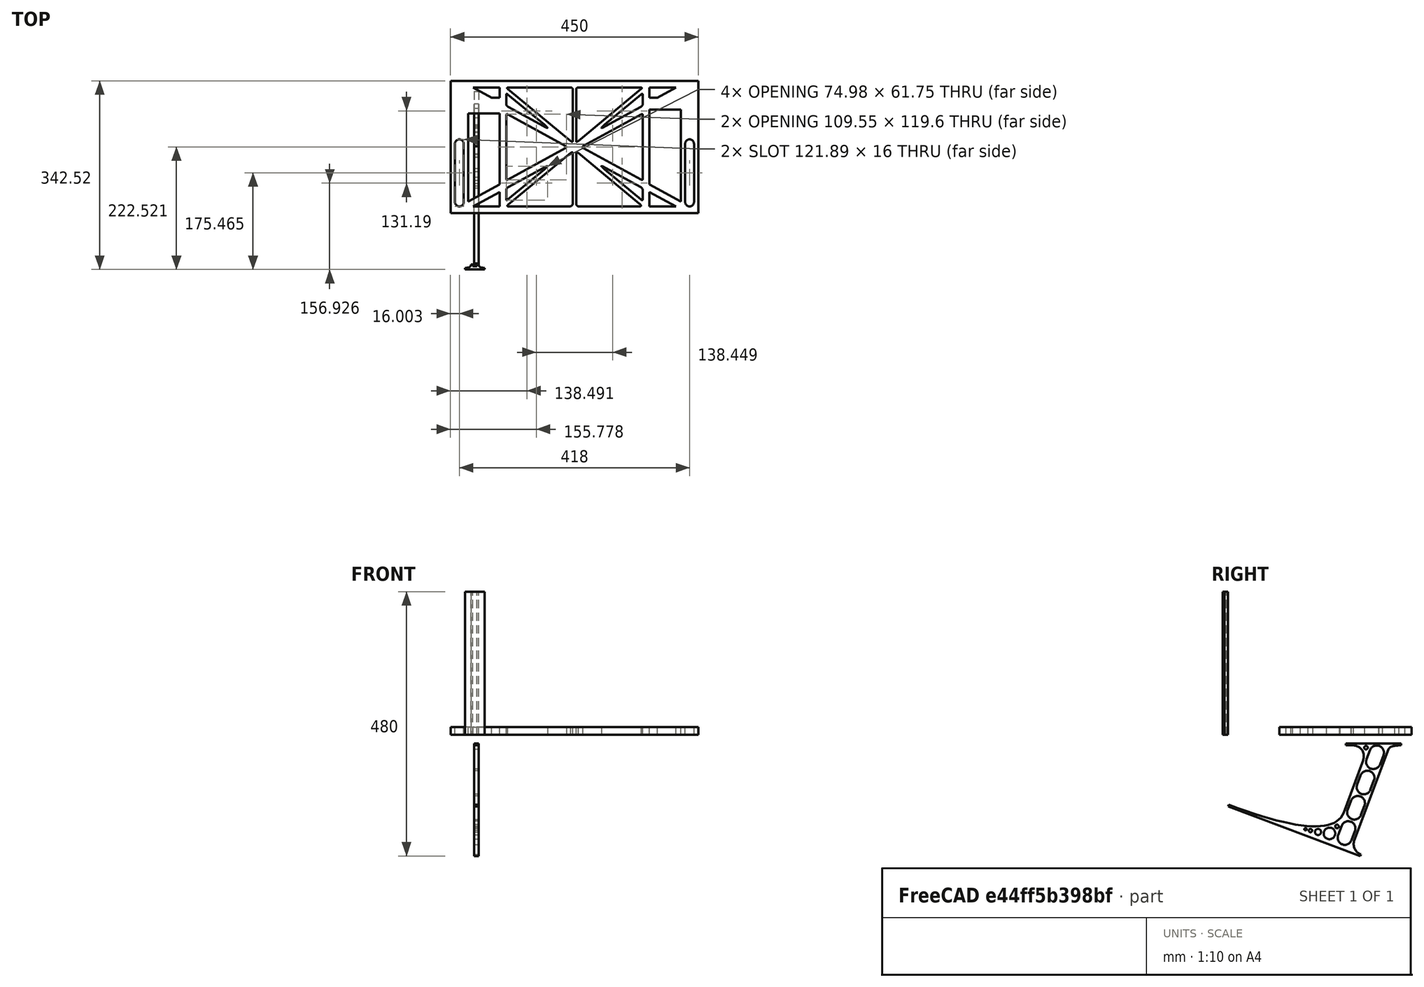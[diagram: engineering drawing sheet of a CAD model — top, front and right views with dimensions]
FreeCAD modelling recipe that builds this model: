
FCSTD DOCUMENT  (FreeCAD 0.19R0.19.2)
Label: laptopStand098
License: All rights reserved
LicenseURL: http://en.wikipedia.org/wiki/All_rights_reserved
objects: Sketcher::SketchObject×3, Part::Extrusion×3
note: 6 computed .brp shape members not serialized (recipe doc carries the construction recipe); baked Part::Feature solids carry a one-line shape summary decoded from their .brp

FEATURE [Sketcher::SketchObject] Sketch
  FullyConstrained = false
  sketch-geometry (276):
    g0: LineSegment StartX=-10.9272 StartY=-82.7794 StartZ=0 EndX=46.0728 EndY=-51.4823 EndZ=0
    g1: LineSegment StartX=366.073 StartY=-91.7794 StartZ=0 EndX=318.073 EndY=-65.424 EndZ=0
    g2: LineSegment StartX=-10.9272 StartY=77.3346 StartZ=0 EndX=-10.9272 EndY=-82.7794 EndZ=0
    g3: LineSegment StartX=375.073 StartY=-82.7794 StartZ=0 EndX=375.073 EndY=83.9235 EndZ=0
    g4: LineSegment StartX=-1.92719 StartY=-91.7794 StartZ=0 EndX=46.0728 EndY=-91.7794 EndZ=0
    g5: LineSegment StartX=318.073 StartY=124.221 StartZ=0 EndX=366.073 EndY=124.221 EndZ=0
    g6: LineSegment StartX=318.073 StartY=83.9235 StartZ=0 EndX=318.073 EndY=-51.4823 EndZ=0
    g7: LineSegment StartX=318.073 StartY=-51.4823 StartZ=0 EndX=375.073 EndY=-82.7794 EndZ=0
    g8: LineSegment StartX=318.073 StartY=-65.424 StartZ=0 EndX=318.073 EndY=-91.7794 EndZ=0
    g9: LineSegment StartX=318.073 StartY=-91.7794 StartZ=0 EndX=366.073 EndY=-91.7794 EndZ=0
    g10: LineSegment StartX=46.0728 StartY=-65.424 StartZ=0 EndX=-1.92719 EndY=-91.7794 EndZ=0
    g11: LineSegment StartX=46.0728 StartY=-65.424 StartZ=0 EndX=46.0728 EndY=-91.7794 EndZ=0
    g12: LineSegment StartX=46.0728 StartY=77.3346 StartZ=0 EndX=46.0728 EndY=-51.4823 EndZ=0
    g13: LineSegment StartX=-42.9272 StartY=136.221 StartZ=0 EndX=-42.9272 EndY=-103.779 EndZ=0
    g14: LineSegment StartX=407.073 StartY=136.221 StartZ=0 EndX=407.073 EndY=-103.779 EndZ=0
    g15: ArcOfCircle CenterX=-26.9272 CenterY=22.1087 CenterZ=0 NormalX=0 NormalY=0 NormalZ=1 AngleXU=0 Radius=8 StartAngle=1e-16 EndAngle=3.14159
    g16: ArcOfCircle CenterX=-26.9272 CenterY=-83.7794 CenterZ=0 NormalX=0 NormalY=0 NormalZ=1 AngleXU=0 Radius=8 StartAngle=3.14159 EndAngle=6.28319
    g17: LineSegment StartX=-34.9272 StartY=22.1087 StartZ=0 EndX=-34.9272 EndY=-83.7794 EndZ=0
    g18: LineSegment StartX=-18.9272 StartY=22.1087 StartZ=0 EndX=-18.9272 EndY=-83.7794 EndZ=0
    g19: ArcOfCircle CenterX=391.073 CenterY=22.1087 CenterZ=0 NormalX=0 NormalY=0 NormalZ=1 AngleXU=0 Radius=8 StartAngle=-4.4e-15 EndAngle=3.14159
    g20: LineSegment StartX=399.073 StartY=22.1087 StartZ=0 EndX=399.073 EndY=-83.7794 EndZ=0
    g21: LineSegment StartX=383.073 StartY=22.1087 StartZ=0 EndX=383.073 EndY=-83.7794 EndZ=0
    g22: ArcOfCircle CenterX=391.073 CenterY=-83.7794 CenterZ=0 NormalX=0 NormalY=0 NormalZ=1 AngleXU=0 Radius=8 StartAngle=3.14159 EndAngle=6.28319
    g23: Circle CenterX=175.022 CenterY=27.0628 CenterZ=0 NormalX=0 NormalY=0 NormalZ=1 AngleXU=0 Radius=1
    g24: Circle CenterX=179.022 CenterY=24.8665 CenterZ=0 NormalX=0 NormalY=0 NormalZ=1 AngleXU=0 Radius=1
    g25: Circle CenterX=179.022 CenterY=27.0628 CenterZ=0 NormalX=0 NormalY=0 NormalZ=1 AngleXU=0 Radius=1
    g26: BSplineCurve PolesCount=3 KnotsCount=2 Degree=2 IsPeriodic=0
    g27: GeomPoint X=175.022 Y=27.0628 Z=0
    g28: GeomPoint X=179.022 Y=27.0628 Z=0
    g29: Circle CenterX=189.124 CenterY=27.0628 CenterZ=0 NormalX=0 NormalY=0 NormalZ=1 AngleXU=0 Radius=1
    g30: Circle CenterX=185.124 CenterY=24.8665 CenterZ=0 NormalX=0 NormalY=0 NormalZ=1 AngleXU=0 Radius=1
    g31: Circle CenterX=185.124 CenterY=27.0628 CenterZ=0 NormalX=0 NormalY=0 NormalZ=1 AngleXU=0 Radius=1
    g32: BSplineCurve PolesCount=3 KnotsCount=2 Degree=2 IsPeriodic=0
    g33: GeomPoint X=189.124 Y=27.0628 Z=0
    g34: GeomPoint X=185.124 Y=27.0628 Z=0
    g35: Circle CenterX=175.022 CenterY=5.37834 CenterZ=0 NormalX=0 NormalY=0 NormalZ=1 AngleXU=0 Radius=1
    g36: Circle CenterX=179.022 CenterY=7.57463 CenterZ=0 NormalX=0 NormalY=0 NormalZ=1 AngleXU=0 Radius=1
    g37: Circle CenterX=179.022 CenterY=5.34704 CenterZ=0 NormalX=0 NormalY=0 NormalZ=1 AngleXU=0 Radius=1
    g38: BSplineCurve PolesCount=3 KnotsCount=2 Degree=2 IsPeriodic=0
    g39: GeomPoint X=175.022 Y=5.37834 Z=0
    g40: GeomPoint X=179.022 Y=5.34704 Z=0
    g41: Circle CenterX=189.124 CenterY=5.37834 CenterZ=0 NormalX=0 NormalY=0 NormalZ=1 AngleXU=0 Radius=1
    g42: Circle CenterX=185.124 CenterY=7.57463 CenterZ=0 NormalX=0 NormalY=0 NormalZ=1 AngleXU=0 Radius=1
    g43: Circle CenterX=185.124 CenterY=5.34704 CenterZ=0 NormalX=0 NormalY=0 NormalZ=1 AngleXU=0 Radius=1
    g44: BSplineCurve PolesCount=3 KnotsCount=2 Degree=2 IsPeriodic=0
    g45: GeomPoint X=189.124 Y=5.37834 Z=0
    g46: GeomPoint X=185.124 Y=5.34704 Z=0
    g47: Circle CenterX=165.871 CenterY=18.1458 CenterZ=0 NormalX=0 NormalY=0 NormalZ=1 AngleXU=0 Radius=1
    g48: Circle CenterX=169.377 CenterY=16.2206 CenterZ=0 NormalX=0 NormalY=0 NormalZ=1 AngleXU=0 Radius=1
    g49: Circle CenterX=165.871 CenterY=14.2954 CenterZ=0 NormalX=0 NormalY=0 NormalZ=1 AngleXU=0 Radius=1
    g50: BSplineCurve PolesCount=3 KnotsCount=2 Degree=2 IsPeriodic=0
    g51: GeomPoint X=165.871 Y=18.1458 Z=0
    g52: GeomPoint X=165.871 Y=14.2954 Z=0
    g53: Circle CenterX=198.275 CenterY=18.1458 CenterZ=0 NormalX=0 NormalY=0 NormalZ=1 AngleXU=0 Radius=1
    g54: Circle CenterX=194.768 CenterY=16.2206 CenterZ=0 NormalX=0 NormalY=0 NormalZ=1 AngleXU=0 Radius=1
    g55: Circle CenterX=198.275 CenterY=14.2954 CenterZ=0 NormalX=0 NormalY=0 NormalZ=1 AngleXU=0 Radius=1
    g56: BSplineCurve PolesCount=3 KnotsCount=2 Degree=2 IsPeriodic=0
    g57: GeomPoint X=198.275 Y=18.1458 Z=0
    g58: GeomPoint X=198.275 Y=14.2954 Z=0
    g59: LineSegment StartX=407.073 StartY=-103.779 StartZ=0 EndX=-42.9272 EndY=-103.779 EndZ=0
    g60: LineSegment StartX=407.073 StartY=136.221 StartZ=0 EndX=-42.9272 EndY=136.221 EndZ=0
    g61: LineSegment StartX=46.0728 StartY=77.3346 StartZ=0 EndX=-10.9272 EndY=77.3346 EndZ=0
    g62: LineSegment StartX=46.0728 StartY=105.865 StartZ=0 EndX=31.5028 EndY=105.865 EndZ=0
    g63: LineSegment StartX=46.0728 StartY=124.221 StartZ=0 EndX=46.0728 EndY=105.865 EndZ=0
    g64: LineSegment StartX=-1.92719 StartY=124.221 StartZ=0 EndX=31.5028 EndY=105.865 EndZ=0
    g65: LineSegment StartX=46.0728 StartY=124.221 StartZ=0 EndX=-1.92719 EndY=124.221 EndZ=0
    g66: LineSegment StartX=318.073 StartY=83.9235 StartZ=0 EndX=375.073 EndY=83.9235 EndZ=0
    g67: Circle CenterX=125.607 CenterY=54.1951 CenterZ=0 NormalX=0 NormalY=0 NormalZ=1 AngleXU=0 Radius=1
    g68: Circle CenterX=139.632 CenterY=46.4944 CenterZ=0 NormalX=0 NormalY=0 NormalZ=1 AngleXU=0 Radius=1
    g69: Circle CenterX=127.326 CenterY=56.7187 CenterZ=0 NormalX=0 NormalY=0 NormalZ=1 AngleXU=0 Radius=1
    g70: BSplineCurve PolesCount=3 KnotsCount=2 Degree=2 IsPeriodic=0
    g71: GeomPoint X=125.607 Y=54.1951 Z=0
    g72: GeomPoint X=127.326 Y=56.7187 Z=0
    g73: Circle CenterX=236.821 CenterY=56.7187 CenterZ=0 NormalX=0 NormalY=0 NormalZ=1 AngleXU=0 Radius=1
    g74: Circle CenterX=224.513 CenterY=46.4944 CenterZ=0 NormalX=0 NormalY=0 NormalZ=1 AngleXU=0 Radius=1
    g75: Circle CenterX=238.538 CenterY=54.1951 CenterZ=0 NormalX=0 NormalY=0 NormalZ=1 AngleXU=0 Radius=1
    g76: BSplineCurve PolesCount=3 KnotsCount=2 Degree=2 IsPeriodic=0
    g77: GeomPoint X=236.821 Y=56.7187 Z=0
    g78: GeomPoint X=238.538 Y=54.1951 Z=0
    g79: Circle CenterX=238.538 CenterY=-21.7539 CenterZ=0 NormalX=0 NormalY=0 NormalZ=1 AngleXU=0 Radius=1
    g80: Circle CenterX=224.513 CenterY=-14.0532 CenterZ=0 NormalX=0 NormalY=0 NormalZ=1 AngleXU=0 Radius=1
    g81: Circle CenterX=236.821 CenterY=-24.2775 CenterZ=0 NormalX=0 NormalY=0 NormalZ=1 AngleXU=0 Radius=1
    g82: BSplineCurve PolesCount=3 KnotsCount=2 Degree=2 IsPeriodic=0
    g83: GeomPoint X=238.538 Y=-21.7539 Z=0
    g84: GeomPoint X=236.821 Y=-24.2775 Z=0
    g85: Circle CenterX=125.607 CenterY=-21.7539 CenterZ=0 NormalX=0 NormalY=0 NormalZ=1 AngleXU=0 Radius=1
    g86: Circle CenterX=139.632 CenterY=-14.0532 CenterZ=0 NormalX=0 NormalY=0 NormalZ=1 AngleXU=0 Radius=1
    g87: Circle CenterX=127.325 CenterY=-24.2775 CenterZ=0 NormalX=0 NormalY=0 NormalZ=1 AngleXU=0 Radius=1
    g88: BSplineCurve PolesCount=3 KnotsCount=2 Degree=2 IsPeriodic=0
    g89: GeomPoint X=125.607 Y=-21.7539 Z=0
    g90: GeomPoint X=127.325 Y=-24.2775 Z=0
    g91: Circle CenterX=302.996 CenterY=111.695 CenterZ=0 NormalX=0 NormalY=0 NormalZ=1 AngleXU=0 Radius=1
    g92: Circle CenterX=306.073 CenterY=114.251 CenterZ=0 NormalX=0 NormalY=0 NormalZ=1 AngleXU=0 Radius=1
    g93: Circle CenterX=306.073 CenterY=110.251 CenterZ=0 NormalX=0 NormalY=0 NormalZ=1 AngleXU=0 Radius=1
    g94: BSplineCurve PolesCount=3 KnotsCount=2 Degree=2 IsPeriodic=0
    g95: GeomPoint X=302.996 Y=111.695 Z=0
    g96: GeomPoint X=306.073 Y=110.251 Z=0
    g97: Circle CenterX=306.073 CenterY=95.2763 CenterZ=0 NormalX=0 NormalY=0 NormalZ=1 AngleXU=0 Radius=1
    g98: Circle CenterX=306.073 CenterY=91.2763 CenterZ=0 NormalX=0 NormalY=0 NormalZ=1 AngleXU=0 Radius=1
    g99: Circle CenterX=302.567 CenterY=89.3511 CenterZ=0 NormalX=0 NormalY=0 NormalZ=1 AngleXU=0 Radius=1
    g100: BSplineCurve PolesCount=3 KnotsCount=2 Degree=2 IsPeriodic=0
    g101: GeomPoint X=306.073 Y=95.2763 Z=0
    g102: GeomPoint X=302.567 Y=89.3511 Z=0
    g103: LineSegment StartX=306.073 StartY=110.251 StartZ=0 EndX=306.073 EndY=95.2763 EndZ=0
    g104: LineSegment StartX=302.996 StartY=111.695 StartZ=0 EndX=236.821 EndY=56.7187 EndZ=0
    g105: LineSegment StartX=238.538 StartY=54.1951 StartZ=0 EndX=302.567 EndY=89.3511 EndZ=0
    g106: Circle CenterX=61.1496 CenterY=111.695 CenterZ=0 NormalX=0 NormalY=0 NormalZ=1 AngleXU=0 Radius=1
    g107: Circle CenterX=58.0728 CenterY=114.251 CenterZ=0 NormalX=0 NormalY=0 NormalZ=1 AngleXU=0 Radius=1
    g108: Circle CenterX=58.0728 CenterY=110.251 CenterZ=0 NormalX=0 NormalY=0 NormalZ=1 AngleXU=0 Radius=1
    g109: BSplineCurve PolesCount=3 KnotsCount=2 Degree=2 IsPeriodic=0
    g110: GeomPoint X=61.1496 Y=111.695 Z=0
    g111: GeomPoint X=58.0728 Y=110.251 Z=0
    g112: Circle CenterX=61.5791 CenterY=89.3511 CenterZ=0 NormalX=0 NormalY=0 NormalZ=1 AngleXU=0 Radius=1
    g113: Circle CenterX=58.0728 CenterY=91.2763 CenterZ=0 NormalX=0 NormalY=0 NormalZ=1 AngleXU=0 Radius=1
    g114: Circle CenterX=58.0728 CenterY=95.2763 CenterZ=0 NormalX=0 NormalY=0 NormalZ=1 AngleXU=0 Radius=1
    g115: BSplineCurve PolesCount=3 KnotsCount=2 Degree=2 IsPeriodic=0
    g116: GeomPoint X=61.5791 Y=89.3511 Z=0
    g117: GeomPoint X=58.0728 Y=95.2763 Z=0
    g118: LineSegment StartX=58.0728 StartY=110.251 StartZ=0 EndX=58.0728 EndY=95.2763 EndZ=0
    g119: LineSegment StartX=61.1496 StartY=111.695 StartZ=0 EndX=127.326 EndY=56.7187 EndZ=0
    g120: LineSegment StartX=125.607 StartY=54.1951 StartZ=0 EndX=61.5791 EndY=89.3511 EndZ=0
    g121: Circle CenterX=61.5791 CenterY=-56.9099 CenterZ=0 NormalX=0 NormalY=0 NormalZ=1 AngleXU=0 Radius=1
    g122: Circle CenterX=58.0728 CenterY=-58.8351 CenterZ=0 NormalX=0 NormalY=0 NormalZ=1 AngleXU=0 Radius=1
    g123: Circle CenterX=58.0728 CenterY=-62.8351 CenterZ=0 NormalX=0 NormalY=0 NormalZ=1 AngleXU=0 Radius=1
    g124: BSplineCurve PolesCount=3 KnotsCount=2 Degree=2 IsPeriodic=0
    g125: GeomPoint X=61.5791 Y=-56.9099 Z=0
    g126: GeomPoint X=58.0728 Y=-62.8351 Z=0
    g127: Circle CenterX=58.0728 CenterY=-77.8102 CenterZ=0 NormalX=0 NormalY=0 NormalZ=1 AngleXU=0 Radius=1
    g128: Circle CenterX=58.0728 CenterY=-81.8102 CenterZ=0 NormalX=0 NormalY=0 NormalZ=1 AngleXU=0 Radius=1
    g129: Circle CenterX=61.1496 CenterY=-79.2541 CenterZ=0 NormalX=0 NormalY=0 NormalZ=1 AngleXU=0 Radius=1
    g130: BSplineCurve PolesCount=3 KnotsCount=2 Degree=2 IsPeriodic=0
    g131: GeomPoint X=58.0728 Y=-77.8102 Z=0
    g132: GeomPoint X=61.1496 Y=-79.2541 Z=0
    g133: LineSegment StartX=58.0728 StartY=-62.8351 StartZ=0 EndX=58.0728 EndY=-77.8102 EndZ=0
    g134: LineSegment StartX=61.1496 StartY=-79.2541 StartZ=0 EndX=127.325 EndY=-24.2775 EndZ=0
    g135: LineSegment StartX=125.607 StartY=-21.7539 StartZ=0 EndX=61.5791 EndY=-56.9099 EndZ=0
    g136: Circle CenterX=302.567 CenterY=-56.9099 CenterZ=0 NormalX=0 NormalY=0 NormalZ=1 AngleXU=0 Radius=1
    g137: Circle CenterX=306.073 CenterY=-58.8351 CenterZ=0 NormalX=0 NormalY=0 NormalZ=1 AngleXU=0 Radius=1
    g138: Circle CenterX=306.073 CenterY=-62.8351 CenterZ=0 NormalX=0 NormalY=0 NormalZ=1 AngleXU=0 Radius=1
    g139: BSplineCurve PolesCount=3 KnotsCount=2 Degree=2 IsPeriodic=0
    g140: GeomPoint X=302.567 Y=-56.9099 Z=0
    g141: GeomPoint X=306.073 Y=-62.8351 Z=0
    g142: Circle CenterX=302.996 CenterY=-79.2541 CenterZ=0 NormalX=0 NormalY=0 NormalZ=1 AngleXU=0 Radius=1
    g143: Circle CenterX=306.073 CenterY=-81.8102 CenterZ=0 NormalX=0 NormalY=0 NormalZ=1 AngleXU=0 Radius=1
    g144: Circle CenterX=306.073 CenterY=-77.8102 CenterZ=0 NormalX=0 NormalY=0 NormalZ=1 AngleXU=0 Radius=1
    g145: BSplineCurve PolesCount=3 KnotsCount=2 Degree=2 IsPeriodic=0
    g146: GeomPoint X=302.996 Y=-79.2541 Z=0
    g147: GeomPoint X=306.073 Y=-77.8102 Z=0
    g148: LineSegment StartX=306.073 StartY=-62.8351 StartZ=0 EndX=306.073 EndY=-77.8102 EndZ=0
    g149: LineSegment StartX=302.996 StartY=-79.2541 StartZ=0 EndX=236.821 EndY=-24.2775 EndZ=0
    g150: LineSegment StartX=238.538 StartY=-21.7539 StartZ=0 EndX=302.567 EndY=-56.9099 EndZ=0
    g151: Circle CenterX=61.6457 CenterY=-88.8112 CenterZ=0 NormalX=0 NormalY=0 NormalZ=1 AngleXU=0 Radius=1
    g152: Circle CenterX=58.0728 CenterY=-91.7794 CenterZ=0 NormalX=0 NormalY=0 NormalZ=1 AngleXU=0 Radius=1
    g153: Circle CenterX=63.9135 CenterY=-91.7794 CenterZ=0 NormalX=0 NormalY=0 NormalZ=1 AngleXU=0 Radius=1
    g154: BSplineCurve PolesCount=3 KnotsCount=2 Degree=2 IsPeriodic=0
    g155: GeomPoint X=61.6457 Y=-88.8112 Z=0
    g156: GeomPoint X=63.9135 Y=-91.7794 Z=0
    g157: Circle CenterX=179.022 CenterY=-85.8163 CenterZ=0 NormalX=0 NormalY=0 NormalZ=1 AngleXU=0 Radius=1
    g158: Circle CenterX=179.022 CenterY=-91.7794 CenterZ=0 NormalX=0 NormalY=0 NormalZ=1 AngleXU=0 Radius=1
    g159: Circle CenterX=171.895 CenterY=-91.7794 CenterZ=0 NormalX=0 NormalY=0 NormalZ=1 AngleXU=0 Radius=1
    g160: BSplineCurve PolesCount=3 KnotsCount=2 Degree=2 IsPeriodic=0
    g161: GeomPoint X=179.022 Y=-85.8163 Z=0
    g162: GeomPoint X=171.895 Y=-91.7794 Z=0
    g163: Circle CenterX=185.124 CenterY=-86.2028 CenterZ=0 NormalX=0 NormalY=0 NormalZ=1 AngleXU=0 Radius=1
    g164: Circle CenterX=185.124 CenterY=-91.7794 CenterZ=0 NormalX=0 NormalY=0 NormalZ=1 AngleXU=0 Radius=1
    g165: Circle CenterX=191.747 CenterY=-91.7794 CenterZ=0 NormalX=0 NormalY=0 NormalZ=1 AngleXU=0 Radius=1
    g166: BSplineCurve PolesCount=3 KnotsCount=2 Degree=2 IsPeriodic=0
    g167: GeomPoint X=185.124 Y=-86.2028 Z=0
    g168: GeomPoint X=191.747 Y=-91.7794 Z=0
    g169: Circle CenterX=299.888 CenterY=-86.6413 CenterZ=0 NormalX=0 NormalY=0 NormalZ=1 AngleXU=0 Radius=1
    g170: Circle CenterX=306.073 CenterY=-91.7794 CenterZ=0 NormalX=0 NormalY=0 NormalZ=1 AngleXU=0 Radius=1
    g171: Circle CenterX=298.776 CenterY=-91.7794 CenterZ=0 NormalX=0 NormalY=0 NormalZ=1 AngleXU=0 Radius=1
    g172: BSplineCurve PolesCount=3 KnotsCount=2 Degree=2 IsPeriodic=0
    g173: GeomPoint X=299.888 Y=-86.6413 Z=0
    g174: GeomPoint X=298.776 Y=-91.7794 Z=0
    g175: LineSegment StartX=189.124 StartY=5.37834 StartZ=0 EndX=299.888 EndY=-86.6413 EndZ=0
    g176: LineSegment StartX=298.776 StartY=-91.7794 StartZ=0 EndX=191.747 EndY=-91.7794 EndZ=0
    g177: LineSegment StartX=185.124 StartY=-86.2028 StartZ=0 EndX=185.124 EndY=5.34704 EndZ=0
    g178: LineSegment StartX=179.022 StartY=5.34704 StartZ=0 EndX=179.022 EndY=-85.8163 EndZ=0
    g179: LineSegment StartX=171.895 StartY=-91.7794 StartZ=0 EndX=63.9135 EndY=-91.7794 EndZ=0
    g180: LineSegment StartX=61.6457 StartY=-88.8112 StartZ=0 EndX=175.022 EndY=5.37834 EndZ=0
    g181: Circle CenterX=302.073 CenterY=124.221 CenterZ=0 NormalX=0 NormalY=0 NormalZ=1 AngleXU=0 Radius=1
    g182: Circle CenterX=306.073 CenterY=124.221 CenterZ=0 NormalX=0 NormalY=0 NormalZ=1 AngleXU=0 Radius=1
    g183: Circle CenterX=302.996 CenterY=121.665 CenterZ=0 NormalX=0 NormalY=0 NormalZ=1 AngleXU=0 Radius=1
    g184: BSplineCurve PolesCount=3 KnotsCount=2 Degree=2 IsPeriodic=0
    g185: GeomPoint X=302.073 Y=124.221 Z=0
    g186: GeomPoint X=302.996 Y=121.665 Z=0
    g187: Circle CenterX=189.124 CenterY=124.221 CenterZ=0 NormalX=0 NormalY=0 NormalZ=1 AngleXU=0 Radius=1
    g188: Circle CenterX=185.124 CenterY=124.221 CenterZ=0 NormalX=0 NormalY=0 NormalZ=1 AngleXU=0 Radius=1
    g189: Circle CenterX=185.124 CenterY=120.221 CenterZ=0 NormalX=0 NormalY=0 NormalZ=1 AngleXU=0 Radius=1
    g190: BSplineCurve PolesCount=3 KnotsCount=2 Degree=2 IsPeriodic=0
    g191: GeomPoint X=189.124 Y=124.221 Z=0
    g192: GeomPoint X=185.124 Y=120.221 Z=0
    g193: Circle CenterX=175.022 CenterY=124.221 CenterZ=0 NormalX=0 NormalY=0 NormalZ=1 AngleXU=0 Radius=1
    g194: Circle CenterX=179.022 CenterY=124.221 CenterZ=0 NormalX=0 NormalY=0 NormalZ=1 AngleXU=0 Radius=1
    g195: Circle CenterX=179.022 CenterY=120.221 CenterZ=0 NormalX=0 NormalY=0 NormalZ=1 AngleXU=0 Radius=1
    g196: BSplineCurve PolesCount=3 KnotsCount=2 Degree=2 IsPeriodic=0
    g197: GeomPoint X=175.022 Y=124.221 Z=0
    g198: GeomPoint X=179.022 Y=120.221 Z=0
    g199: Circle CenterX=62.0728 CenterY=124.221 CenterZ=0 NormalX=0 NormalY=0 NormalZ=1 AngleXU=0 Radius=1
    g200: Circle CenterX=58.0728 CenterY=124.221 CenterZ=0 NormalX=0 NormalY=0 NormalZ=1 AngleXU=0 Radius=1
    g201: Circle CenterX=61.1496 CenterY=121.665 CenterZ=0 NormalX=0 NormalY=0 NormalZ=1 AngleXU=0 Radius=1
    g202: BSplineCurve PolesCount=3 KnotsCount=2 Degree=2 IsPeriodic=0
    g203: GeomPoint X=62.0728 Y=124.221 Z=0
    g204: GeomPoint X=61.1496 Y=121.665 Z=0
    g205: LineSegment StartX=62.0728 StartY=124.221 StartZ=0 EndX=175.022 EndY=124.221 EndZ=0
    g206: LineSegment StartX=179.022 StartY=120.221 StartZ=0 EndX=179.022 EndY=27.0628 EndZ=0
    g207: LineSegment StartX=185.124 StartY=27.0628 StartZ=0 EndX=185.124 EndY=120.221 EndZ=0
    g208: LineSegment StartX=189.124 StartY=124.221 StartZ=0 EndX=302.073 EndY=124.221 EndZ=0
    g209: LineSegment StartX=302.996 StartY=121.665 StartZ=0 EndX=189.124 EndY=27.0628 EndZ=0
    g210: LineSegment StartX=175.022 StartY=27.0628 StartZ=0 EndX=61.1496 EndY=121.665 EndZ=0
    g211: Circle CenterX=61.5791 CenterY=75.4095 CenterZ=0 NormalX=0 NormalY=0 NormalZ=1 AngleXU=0 Radius=1
    g212: Circle CenterX=58.0728 CenterY=77.3346 CenterZ=0 NormalX=0 NormalY=0 NormalZ=1 AngleXU=0 Radius=1
    g213: Circle CenterX=58.0728 CenterY=73.3346 CenterZ=0 NormalX=0 NormalY=0 NormalZ=1 AngleXU=0 Radius=1
    g214: BSplineCurve PolesCount=3 KnotsCount=2 Degree=2 IsPeriodic=0
    g215: GeomPoint X=61.5791 Y=75.4095 Z=0
    g216: GeomPoint X=58.0728 Y=73.3346 Z=0
    g217: Circle CenterX=58.0728 CenterY=-40.8935 CenterZ=0 NormalX=0 NormalY=0 NormalZ=1 AngleXU=0 Radius=1
    g218: Circle CenterX=58.0728 CenterY=-44.8935 CenterZ=0 NormalX=0 NormalY=0 NormalZ=1 AngleXU=0 Radius=1
    g219: Circle CenterX=61.5791 CenterY=-42.9683 CenterZ=0 NormalX=0 NormalY=0 NormalZ=1 AngleXU=0 Radius=1
    g220: BSplineCurve PolesCount=3 KnotsCount=2 Degree=2 IsPeriodic=0
    g221: GeomPoint X=58.0728 Y=-40.8935 Z=0
    g222: GeomPoint X=61.5791 Y=-42.9683 Z=0
    g223: LineSegment StartX=61.5791 StartY=-42.9683 StartZ=0 EndX=165.871 EndY=14.2954 EndZ=0
    g224: LineSegment StartX=165.871 StartY=18.1458 StartZ=0 EndX=61.5791 EndY=75.4095 EndZ=0
    g225: LineSegment StartX=58.0728 StartY=73.3346 StartZ=0 EndX=58.0728 EndY=-40.8935 EndZ=0
    g226: Circle CenterX=302.567 CenterY=-42.9683 CenterZ=0 NormalX=0 NormalY=0 NormalZ=1 AngleXU=0 Radius=1
    g227: Circle CenterX=306.073 CenterY=-44.8935 CenterZ=0 NormalX=0 NormalY=0 NormalZ=1 AngleXU=0 Radius=1
    g228: Circle CenterX=306.073 CenterY=-40.8935 CenterZ=0 NormalX=0 NormalY=0 NormalZ=1 AngleXU=0 Radius=1
    g229: BSplineCurve PolesCount=3 KnotsCount=2 Degree=2 IsPeriodic=0
    g230: GeomPoint X=302.567 Y=-42.9683 Z=0
    g231: GeomPoint X=306.073 Y=-40.8935 Z=0
    g232: Circle CenterX=306.073 CenterY=73.3346 CenterZ=0 NormalX=0 NormalY=0 NormalZ=1 AngleXU=0 Radius=1
    g233: Circle CenterX=306.073 CenterY=77.3346 CenterZ=0 NormalX=0 NormalY=0 NormalZ=1 AngleXU=0 Radius=1
    g234: Circle CenterX=302.567 CenterY=75.4095 CenterZ=0 NormalX=0 NormalY=0 NormalZ=1 AngleXU=0 Radius=1
    g235: BSplineCurve PolesCount=3 KnotsCount=2 Degree=2 IsPeriodic=0
    g236: GeomPoint X=306.073 Y=73.3346 Z=0
    g237: GeomPoint X=302.567 Y=75.4095 Z=0
    g238: LineSegment StartX=302.567 StartY=-42.9683 StartZ=0 EndX=198.275 EndY=14.2954 EndZ=0
    g239: LineSegment StartX=198.275 StartY=18.1458 StartZ=0 EndX=302.567 EndY=75.4095 EndZ=0
    g240: LineSegment StartX=306.073 StartY=73.3346 StartZ=0 EndX=306.073 EndY=-40.8935 EndZ=0
    g241: LineSegment StartX=318.073 StartY=124.221 StartZ=0 EndX=322.073 EndY=124.221 EndZ=0
    g242: LineSegment StartX=366.073 StartY=124.221 StartZ=0 EndX=362.073 EndY=124.221 EndZ=0
    g243: LineSegment StartX=328.643 StartY=105.865 StartZ=0 EndX=332.643 EndY=105.865 EndZ=0
    g244: LineSegment StartX=332.651 StartY=105.853 StartZ=0 EndX=336.157 EndY=107.779 EndZ=0
    g245: LineSegment StartX=366.073 StartY=124.221 StartZ=0 EndX=362.567 EndY=122.294 EndZ=0
    g246: LineSegment StartX=318.073 StartY=105.865 StartZ=0 EndX=318.073 EndY=109.865 EndZ=0
    g247: LineSegment StartX=318.073 StartY=105.865 StartZ=0 EndX=322.073 EndY=105.865 EndZ=0
    g248: LineSegment StartX=318.073 StartY=124.221 StartZ=0 EndX=318.073 EndY=120.221 EndZ=0
    g249: LineSegment StartX=322.073 StartY=105.865 StartZ=0 EndX=328.643 EndY=105.865 EndZ=0
    g250: LineSegment StartX=318.073 StartY=120.221 StartZ=0 EndX=318.073 EndY=109.865 EndZ=0
    g251: LineSegment StartX=336.157 StartY=107.779 StartZ=0 EndX=362.567 EndY=122.294 EndZ=0
    g252: Circle CenterX=362.073 CenterY=124.221 CenterZ=0 NormalX=0 NormalY=0 NormalZ=1 AngleXU=0 Radius=1
    g253: Circle CenterX=366.073 CenterY=124.221 CenterZ=0 NormalX=0 NormalY=0 NormalZ=1 AngleXU=0 Radius=1
    g254: Circle CenterX=362.567 CenterY=122.294 CenterZ=0 NormalX=0 NormalY=0 NormalZ=1 AngleXU=0 Radius=1
    g255: BSplineCurve PolesCount=3 KnotsCount=2 Degree=2 IsPeriodic=0
    g256: GeomPoint X=362.073 Y=124.221 Z=0
    g257: GeomPoint X=362.567 Y=122.294 Z=0
    g258: Circle CenterX=322.073 CenterY=124.221 CenterZ=0 NormalX=0 NormalY=0 NormalZ=1 AngleXU=0 Radius=1
    g259: Circle CenterX=318.073 CenterY=124.221 CenterZ=0 NormalX=0 NormalY=0 NormalZ=1 AngleXU=0 Radius=1
    g260: Circle CenterX=318.073 CenterY=120.221 CenterZ=0 NormalX=0 NormalY=0 NormalZ=1 AngleXU=0 Radius=1
    g261: BSplineCurve PolesCount=3 KnotsCount=2 Degree=2 IsPeriodic=0
    g262: GeomPoint X=322.073 Y=124.221 Z=0
    g263: GeomPoint X=318.073 Y=120.221 Z=0
    g264: Circle CenterX=322.073 CenterY=105.865 CenterZ=0 NormalX=0 NormalY=0 NormalZ=1 AngleXU=0 Radius=1
    g265: Circle CenterX=318.073 CenterY=105.865 CenterZ=0 NormalX=0 NormalY=0 NormalZ=1 AngleXU=0 Radius=1
    g266: Circle CenterX=318.073 CenterY=109.865 CenterZ=0 NormalX=0 NormalY=0 NormalZ=1 AngleXU=0 Radius=1
    g267: BSplineCurve PolesCount=3 KnotsCount=2 Degree=2 IsPeriodic=0
    g268: GeomPoint X=322.073 Y=105.865 Z=0
    g269: GeomPoint X=318.073 Y=109.865 Z=0
    g270: Circle CenterX=336.157 CenterY=107.779 CenterZ=0 NormalX=0 NormalY=0 NormalZ=1 AngleXU=0 Radius=1
    g271: Circle CenterX=332.651 CenterY=105.853 CenterZ=0 NormalX=0 NormalY=0 NormalZ=1 AngleXU=0 Radius=1
    g272: Circle CenterX=328.643 CenterY=105.865 CenterZ=0 NormalX=0 NormalY=0 NormalZ=1 AngleXU=0 Radius=1
    g273: BSplineCurve PolesCount=3 KnotsCount=2 Degree=2 IsPeriodic=0
    g274: GeomPoint X=336.157 Y=107.779 Z=0
    g275: GeomPoint X=328.643 Y=105.865 Z=0
  constraints (478):
    c: Horizontal(g4)
    c: Coincident(g6,g7)
    c: Coincident(g8,g1)
    c: Tangent(g6,g8)
    c: Coincident(g11,g10)
    c: Coincident(g0,g12)
    c: Block(g7)
    c: Block(g3)
    c: Block(g1)
    c: Block(g8)
    c: Block(g11)
    c: Block(g10)
    c: Block(g0)
    c: Block(g2)
    c: Block(g5)
    c: Block(g9)
    c: Block(g4)
    c: Vertical(g13)
    c: Vertical(g14)
    c: Block(g14)
    c: Block(g13)
    c: Tangent(g15,g18) = 1.5708
    c: Tangent(g15,g17) = -1.5708
    c: Tangent(g17,g16) = -1.5708
    c: Tangent(g18,g16) = 1.5708
    c: Vertical(g17)
    c: Equal(g15,g16)
    c: Block(g18)
    c: Block(g17)
    c: Tangent(g19,g20) = 1.5708
    c: Tangent(g20,g22) = 1.5708
    c: Equal(g19,g22)
    c: Coincident(g21,g19)
    c: Coincident(g21,g22)
    c: Block(g20)
    c: Block(g21)
    c: Weight(g23) = 1
    c: Equal(g23,g24)
    c: Equal(g23,g25)
    c: InternalAlignment(g23,g26)
    c: InternalAlignment(g24,g26)
    c: InternalAlignment(g25,g26)
    c: InternalAlignment(g27,g26)
    c: InternalAlignment(g28,g26)
    c: Weight(g29) = 1
    c: Equal(g29,g30)
    c: Equal(g29,g31)
    c: InternalAlignment(g29,g32)
    c: InternalAlignment(g30,g32)
    c: InternalAlignment(g31,g32)
    c: InternalAlignment(g33,g32)
    c: InternalAlignment(g34,g32)
    c: Block(g32)
    c: Block(g26)
    c: Weight(g35) = 1
    c: Equal(g35,g36)
    c: Equal(g35,g37)
    c: InternalAlignment(g35,g38)
    c: InternalAlignment(g36,g38)
    c: InternalAlignment(g37,g38)
    c: InternalAlignment(g39,g38)
    c: InternalAlignment(g40,g38)
    c: Weight(g41) = 1
    c: Equal(g41,g42)
    c: Equal(g41,g43)
    c: InternalAlignment(g41,g44)
    c: InternalAlignment(g42,g44)
    c: InternalAlignment(g43,g44)
    c: InternalAlignment(g45,g44)
    c: InternalAlignment(g46,g44)
    c: Block(g44)
    c: Block(g38)
    c: Weight(g47) = 1
    c: Equal(g47,g48)
    c: Equal(g47,g49)
    c: InternalAlignment(g47,g50)
    c: InternalAlignment(g48,g50)
    c: InternalAlignment(g49,g50)
    c: InternalAlignment(g51,g50)
    c: InternalAlignment(g52,g50)
    c: Weight(g53) = 1
    c: Equal(g53,g54)
    c: Equal(g53,g55)
    c: InternalAlignment(g53,g56)
    c: InternalAlignment(g54,g56)
    c: InternalAlignment(g55,g56)
    c: InternalAlignment(g57,g56)
    c: InternalAlignment(g58,g56)
    c: Block(g50)
    c: Block(g56)
    c: Coincident(g59,g14)
    c: Coincident(g59,g13)
    c: Horizontal(g59)
    c: Distance(g59) = 450
    c: Coincident(g60,g14)
    c: Coincident(g60,g13)
    c: Horizontal(g60)
    c: Horizontal(g61)
    c: Coincident(g12,g61)
    c: Horizontal(g62)
    c: Vertical(g63)
    c: Block(g63)
    c: Block(g62)
    c: Block(g61)
    c: Distance(g63) = 18.3554
    c: Coincident(g65,g63)
    c: Coincident(g65,g64)
    c: Horizontal(g65)
    c: Block(g65)
    c: Block(g64)
    c: Coincident(g62,g64)
    c: Coincident(g2,g61)
    c: Coincident(g66,g6)
    c: Horizontal(g66)
    c: Block(g66)
    c: Coincident(g3,g66)
    c: Weight(g67) = 1
    c: Equal(g67,g68)
    c: Equal(g67,g69)
    c: InternalAlignment(g67,g70)
    c: InternalAlignment(g68,g70)
    c: InternalAlignment(g69,g70)
    c: InternalAlignment(g71,g70)
    c: InternalAlignment(g72,g70)
    c: Block(g70)
    c: Weight(g73) = 1
    c: Equal(g73,g74)
    c: Equal(g73,g75)
    c: InternalAlignment(g73,g76)
    c: InternalAlignment(g74,g76)
    c: InternalAlignment(g75,g76)
    c: InternalAlignment(g77,g76)
    c: InternalAlignment(g78,g76)
    c: Block(g76)
    c: Weight(g79) = 1
    c: Equal(g79,g80)
    c: Equal(g79,g81)
    c: InternalAlignment(g79,g82)
    c: InternalAlignment(g80,g82)
    c: InternalAlignment(g81,g82)
    c: InternalAlignment(g83,g82)
    c: InternalAlignment(g84,g82)
    c: Block(g82)
    c: Weight(g85) = 1
    c: Equal(g85,g86)
    c: Equal(g85,g87)
    c: InternalAlignment(g85,g88)
    c: InternalAlignment(g86,g88)
    c: InternalAlignment(g87,g88)
    c: InternalAlignment(g89,g88)
    c: InternalAlignment(g90,g88)
    c: Block(g88)
    c: Weight(g91) = 1
    c: Equal(g91,g92)
    c: Equal(g91,g93)
    c: InternalAlignment(g91,g94)
    c: InternalAlignment(g92,g94)
    c: InternalAlignment(g93,g94)
    c: InternalAlignment(g95,g94)
    c: InternalAlignment(g96,g94)
    c: Weight(g97) = 1
    c: Equal(g97,g98)
    c: Equal(g97,g99)
    c: InternalAlignment(g97,g100)
    c: InternalAlignment(g98,g100)
    c: InternalAlignment(g99,g100)
    c: InternalAlignment(g101,g100)
    c: InternalAlignment(g102,g100)
    c: Block(g94)
    c: Block(g100)
    c: Coincident(g103,g94)
    c: Coincident(g103,g100)
    c: Vertical(g103)
    c: Coincident(g104,g94)
    c: Coincident(g104,g76)
    c: Coincident(g105,g76)
    c: Coincident(g105,g100)
    c: Weight(g106) = 1
    c: Equal(g106,g107)
    c: Equal(g106,g108)
    c: InternalAlignment(g106,g109)
    c: InternalAlignment(g107,g109)
    c: InternalAlignment(g108,g109)
    c: InternalAlignment(g110,g109)
    c: InternalAlignment(g111,g109)
    c: Weight(g112) = 1
    c: Equal(g112,g113)
    c: Equal(g112,g114)
    c: InternalAlignment(g112,g115)
    c: InternalAlignment(g113,g115)
    c: InternalAlignment(g114,g115)
    c: InternalAlignment(g116,g115)
    c: InternalAlignment(g117,g115)
    c: Block(g109)
    c: Block(g115)
    c: Coincident(g118,g109)
    c: Coincident(g118,g115)
    c: Vertical(g118)
    c: Coincident(g119,g109)
    c: Coincident(g119,g70)
    c: Coincident(g120,g70)
    c: Coincident(g120,g115)
    c: Weight(g121) = 1
    c: Equal(g121,g122)
    c: Equal(g121,g123)
    c: InternalAlignment(g121,g124)
    c: InternalAlignment(g122,g124)
    c: InternalAlignment(g123,g124)
    c: InternalAlignment(g125,g124)
    c: InternalAlignment(g126,g124)
    c: Weight(g127) = 1
    c: Equal(g127,g128)
    c: Equal(g127,g129)
    c: InternalAlignment(g127,g130)
    c: InternalAlignment(g128,g130)
    c: InternalAlignment(g129,g130)
    c: InternalAlignment(g131,g130)
    c: InternalAlignment(g132,g130)
    c: Block(g124)
    c: Block(g130)
    c: Coincident(g133,g124)
    c: Coincident(g133,g130)
    c: Vertical(g133)
    c: Coincident(g134,g130)
    c: Coincident(g134,g88)
    c: Coincident(g135,g88)
    c: Coincident(g135,g124)
    c: Weight(g136) = 1
    c: Equal(g136,g137)
    c: Equal(g136,g138)
    c: InternalAlignment(g136,g139)
    c: InternalAlignment(g137,g139)
    c: InternalAlignment(g138,g139)
    c: InternalAlignment(g140,g139)
    c: InternalAlignment(g141,g139)
    c: Weight(g142) = 1
    c: Equal(g142,g143)
    c: Equal(g142,g144)
    c: InternalAlignment(g142,g145)
    c: InternalAlignment(g143,g145)
    c: InternalAlignment(g144,g145)
    c: InternalAlignment(g146,g145)
    c: InternalAlignment(g147,g145)
    c: Block(g139)
    c: Block(g145)
    c: Coincident(g148,g139)
    c: Coincident(g148,g145)
    c: Vertical(g148)
    c: Coincident(g149,g145)
    c: Coincident(g149,g82)
    c: Coincident(g150,g82)
    c: Coincident(g150,g139)
    c: Weight(g151) = 1
    c: Equal(g151,g152)
    c: Equal(g151,g153)
    c: InternalAlignment(g151,g154)
    c: InternalAlignment(g152,g154)
    c: InternalAlignment(g153,g154)
    c: InternalAlignment(g155,g154)
    c: InternalAlignment(g156,g154)
    c: Weight(g157) = 1
    c: Equal(g157,g158)
    c: Equal(g157,g159)
    c: InternalAlignment(g157,g160)
    c: InternalAlignment(g158,g160)
    c: InternalAlignment(g159,g160)
    c: InternalAlignment(g161,g160)
    c: InternalAlignment(g162,g160)
    c: Weight(g163) = 1
    c: Equal(g163,g164)
    c: Equal(g163,g165)
    c: InternalAlignment(g163,g166)
    c: InternalAlignment(g164,g166)
    c: InternalAlignment(g165,g166)
    c: InternalAlignment(g167,g166)
    c: InternalAlignment(g168,g166)
    c: Weight(g169) = 1
    c: Equal(g169,g170)
    c: Equal(g169,g171)
    c: InternalAlignment(g169,g172)
    c: InternalAlignment(g170,g172)
    c: InternalAlignment(g171,g172)
    c: InternalAlignment(g173,g172)
    c: InternalAlignment(g174,g172)
    c: Block(g172)
    c: Block(g166)
    c: Block(g160)
    c: Block(g154)
    c: Coincident(g175,g44)
    c: Coincident(g175,g172)
    c: Coincident(g176,g172)
    c: Coincident(g176,g166)
    c: Horizontal(g176)
    c: Coincident(g177,g166)
    c: Coincident(g177,g44)
    c: Vertical(g177)
    c: Coincident(g178,g38)
    c: Coincident(g178,g160)
    c: Vertical(g178)
    c: Coincident(g179,g160)
    c: Coincident(g179,g154)
    c: Horizontal(g179)
    c: Coincident(g180,g154)
    c: Coincident(g180,g38)
    c: Weight(g181) = 1
    c: Equal(g181,g182)
    c: Equal(g181,g183)
    c: InternalAlignment(g181,g184)
    c: InternalAlignment(g182,g184)
    c: InternalAlignment(g183,g184)
    c: InternalAlignment(g185,g184)
    c: InternalAlignment(g186,g184)
    c: Weight(g187) = 1
    c: Equal(g187,g188)
    c: Equal(g187,g189)
    c: InternalAlignment(g187,g190)
    c: InternalAlignment(g188,g190)
    c: InternalAlignment(g189,g190)
    c: InternalAlignment(g191,g190)
    c: InternalAlignment(g192,g190)
    c: Weight(g193) = 1
    c: Equal(g193,g194)
    c: Equal(g193,g195)
    c: InternalAlignment(g193,g196)
    c: InternalAlignment(g194,g196)
    c: InternalAlignment(g195,g196)
    c: InternalAlignment(g197,g196)
    c: InternalAlignment(g198,g196)
    c: Weight(g199) = 1
    c: Equal(g199,g200)
    c: Equal(g199,g201)
    c: InternalAlignment(g199,g202)
    c: InternalAlignment(g200,g202)
    c: InternalAlignment(g201,g202)
    c: InternalAlignment(g203,g202)
    c: InternalAlignment(g204,g202)
    c: Block(g202)
    c: Block(g196)
    c: Block(g190)
    c: Block(g184)
    c: Coincident(g205,g202)
    c: Coincident(g205,g196)
    c: Horizontal(g205)
    c: Coincident(g206,g196)
    c: Coincident(g206,g26)
    c: Vertical(g206)
    c: Coincident(g207,g32)
    c: Coincident(g207,g190)
    c: Vertical(g207)
    c: Coincident(g208,g190)
    c: Coincident(g208,g184)
    c: Horizontal(g208)
    c: Coincident(g209,g184)
    c: Coincident(g209,g32)
    c: Coincident(g210,g26)
    c: Weight(g211) = 1
    c: Equal(g211,g212)
    c: Equal(g211,g213)
    c: InternalAlignment(g211,g214)
    c: InternalAlignment(g212,g214)
    c: InternalAlignment(g213,g214)
    c: InternalAlignment(g215,g214)
    c: InternalAlignment(g216,g214)
    c: Weight(g217) = 1
    c: Equal(g217,g218)
    c: Equal(g217,g219)
    c: InternalAlignment(g217,g220)
    c: InternalAlignment(g218,g220)
    c: InternalAlignment(g219,g220)
    c: InternalAlignment(g221,g220)
    c: InternalAlignment(g222,g220)
    c: Block(g220)
    c: Block(g214)
    c: Coincident(g223,g220)
    c: Coincident(g223,g50)
    c: Coincident(g224,g50)
    c: Coincident(g224,g214)
    c: Coincident(g225,g214)
    c: Coincident(g225,g220)
    c: Vertical(g225)
    c: Weight(g226) = 1
    c: Equal(g226,g227)
    c: Equal(g226,g228)
    c: InternalAlignment(g226,g229)
    c: InternalAlignment(g227,g229)
    c: InternalAlignment(g228,g229)
    c: InternalAlignment(g230,g229)
    c: InternalAlignment(g231,g229)
    c: Weight(g232) = 1
    c: Equal(g232,g233)
    c: Equal(g232,g234)
    c: InternalAlignment(g232,g235)
    c: InternalAlignment(g233,g235)
    c: InternalAlignment(g234,g235)
    c: InternalAlignment(g236,g235)
    c: InternalAlignment(g237,g235)
    c: Block(g235)
    c: Block(g229)
    c: Coincident(g238,g229)
    c: Coincident(g238,g56)
    c: Coincident(g239,g56)
    c: Coincident(g239,g235)
    c: Coincident(g240,g235)
    c: Coincident(g240,g229)
    c: Vertical(g240)
    c: Horizontal(g241)
    c: Horizontal(g242)
    c: Horizontal(g243)
    c: Vertical(g246)
    c: Horizontal(g247)
    c: Vertical(g248)
    c: Distance(g243) = 4
    c: Distance(g247) = 4
    c: Distance(g246) = 4
    c: Distance(g248) = 4
    c: Distance(g241) = 4
    c: Distance(g242) = 4
    c: Coincident(g241,g5)
    c: Coincident(g248,g5)
    c: Coincident(g5,g242)
    c: Coincident(g249,g247)
    c: Coincident(g249,g243)
    c: Horizontal(g249)
    c: Block(g249)
    c: Coincident(g250,g248)
    c: Coincident(g250,g246)
    c: Vertical(g250)
    c: Block(g250)
    c: Distance(g244) = 4
    c: Distance(g245) = 4
    c: Coincident(g245,g5)
    c: Coincident(g251,g244)
    c: Coincident(g251,g245)
    c: Block(g251)
    c: Coincident(g255,g242)
    c: Weight(g252) = 1
    c: Equal(g252,g253)
    c: Coincident(g253,g5)
    c: Equal(g252,g254)
    c: Coincident(g255,g245)
    c: InternalAlignment(g252,g255)
    c: InternalAlignment(g253,g255)
    c: InternalAlignment(g254,g255)
    c: InternalAlignment(g256,g255)
    c: InternalAlignment(g257,g255)
    c: Coincident(g261,g241)
    c: Weight(g258) = 1
    c: Equal(g258,g259)
    c: Coincident(g259,g5)
    c: Equal(g258,g260)
    c: Coincident(g261,g248)
    c: InternalAlignment(g258,g261)
    c: InternalAlignment(g259,g261)
    c: InternalAlignment(g260,g261)
    c: InternalAlignment(g262,g261)
    c: InternalAlignment(g263,g261)
    c: Coincident(g267,g247)
    c: Weight(g264) = 1
    c: Equal(g264,g265)
    c: Coincident(g265,g246)
    c: Equal(g264,g266)
    c: Coincident(g267,g246)
    c: InternalAlignment(g264,g267)
    c: InternalAlignment(g265,g267)
    c: InternalAlignment(g266,g267)
    c: InternalAlignment(g268,g267)
    c: InternalAlignment(g269,g267)
    c: Coincident(g273,g244)
    c: Weight(g270) = 1
    c: Equal(g270,g271)
    c: Coincident(g271,g244)
    c: Equal(g270,g272)
    c: Coincident(g273,g243)
    c: InternalAlignment(g270,g273)
    c: InternalAlignment(g271,g273)
    c: InternalAlignment(g272,g273)
    c: InternalAlignment(g274,g273)
    c: InternalAlignment(g275,g273)
FEATURE [Sketcher::SketchObject] Sketch001
  FullyConstrained = true
  MapMode = 4
  Placement = pos=(0,0,0) rot=(0.57735,0.57735,0.57735;2.0944rad)
  Support = -> [Sketch]
  sketch-geometry (46):
    g0: BSplineCurve PolesCount=3 KnotsCount=2 Degree=2 IsPeriodic=0
    g1: ArcOfCircle CenterX=73.1223 CenterY=-32.291 CenterZ=0 NormalX=0 NormalY=0 NormalZ=1 AngleXU=0 Radius=13 StartAngle=5.92268 EndAngle=9.06428
    g2: ArcOfCircle CenterX=66.7816 CenterY=-49.1439 CenterZ=0 NormalX=0 NormalY=0 NormalZ=1 AngleXU=0 Radius=13 StartAngle=2.78068 EndAngle=5.92131
    g3: ArcOfCircle CenterX=55.9263 CenterY=-78.1807 CenterZ=0 NormalX=0 NormalY=0 NormalZ=1 AngleXU=0 Radius=13 StartAngle=5.92268 EndAngle=9.06428
    g4: ArcOfCircle CenterX=49.5884 CenterY=-95.0342 CenterZ=0 NormalX=0 NormalY=0 NormalZ=1 AngleXU=0 Radius=13 StartAngle=2.78068 EndAngle=5.92131
    g5: ArcOfCircle CenterX=38.7206 CenterY=-124.067 CenterZ=0 NormalX=0 NormalY=0 NormalZ=1 AngleXU=0 Radius=13 StartAngle=5.92268 EndAngle=9.06428
    g6: ArcOfCircle CenterX=32.3875 CenterY=-140.92 CenterZ=0 NormalX=0 NormalY=0 NormalZ=1 AngleXU=0 Radius=13 StartAngle=2.78068 EndAngle=5.92131
    g7: ArcOfCircle CenterX=21.4715 CenterY=-169.934 CenterZ=0 NormalX=0 NormalY=0 NormalZ=1 AngleXU=0 Radius=13 StartAngle=5.92268 EndAngle=9.06428
    g8: ArcOfCircle CenterX=15.1336 CenterY=-186.787 CenterZ=0 NormalX=0 NormalY=0 NormalZ=1 AngleXU=0 Radius=13 StartAngle=2.78068 EndAngle=5.92131
    g9-g12: Circle x4 (B-spline internal-alignment scaffolding for g13; pole/knot coordinates omitted)
    g13: BSplineCurve PolesCount=4 KnotsCount=2 Degree=3 IsPeriodic=0
    g14: GeomPoint X=28.8094 Y=-19.0875 Z=0
    g15: GeomPoint X=47.0443 Y=-50.4712 Z=0
    g16: Circle CenterX=53.5586 CenterY=-23.2695 CenterZ=0 NormalX=0 NormalY=0 NormalZ=1 AngleXU=0 Radius=3.24518
    g17: Circle CenterX=-195.441 CenterY=-127.082 CenterZ=0 NormalX=0 NormalY=0 NormalZ=1 AngleXU=0 Radius=1
    g18: Circle CenterX=-8.24091 CenterY=-197.481 CenterZ=0 NormalX=0 NormalY=0 NormalZ=1 AngleXU=0 Radius=1
    g19: Circle CenterX=12.8789 CenterY=-141.321 CenterZ=0 NormalX=0 NormalY=0 NormalZ=1 AngleXU=0 Radius=1
    g20: BSplineCurve PolesCount=3 KnotsCount=2 Degree=2 IsPeriodic=0
    g21: GeomPoint X=-195.441 Y=-127.082 Z=0
    g22: GeomPoint X=12.8789 Y=-141.321 Z=0
    g23: Circle CenterX=-12.8016 CenterY=-179.036 CenterZ=0 NormalX=0 NormalY=0 NormalZ=1 AngleXU=0 Radius=10.5072
    g24: Circle CenterX=0.933922 CenterY=-166.43 CenterZ=0 NormalX=0 NormalY=0 NormalZ=1 AngleXU=0 Radius=3.26661
    g25: Circle CenterX=-33.5518 CenterY=-176.44 CenterZ=0 NormalX=0 NormalY=0 NormalZ=1 AngleXU=0 Radius=5.64388
    g26: Circle CenterX=-47.2366 CenterY=-173.859 CenterZ=0 NormalX=0 NormalY=0 NormalZ=1 AngleXU=0 Radius=3.01653
    g27: Circle CenterX=-56.2595 CenterY=-171.456 CenterZ=0 NormalX=0 NormalY=0 NormalZ=1 AngleXU=0 Radius=2.12826
    g28: ArcOfCircle CenterX=51.2151 CenterY=-198.473 CenterZ=0 NormalX=0 NormalY=0 NormalZ=1 AngleXU=0 Radius=20 StartAngle=2.78189 EndAngle=4.35269
    g29: LineSegment StartX=32.4951 StartY=-191.433 StartZ=0 EndX=94.6578 EndY=-26.1352 EndZ=0
    g30: LineSegment StartX=43.1192 StartY=-220.001 StartZ=0 EndX=-196.497 EndY=-129.89 EndZ=0
    g31: LineSegment StartX=43.1192 StartY=-220.001 StartZ=0 EndX=44.1752 EndY=-217.193 EndZ=0
    g32: LineSegment StartX=117.223 StartY=-19.0875 StartZ=0 EndX=117.223 EndY=-16.0875 EndZ=0
    g33: LineSegment StartX=117.223 StartY=-16.0875 StartZ=0 EndX=17.2232 EndY=-16.0875 EndZ=0
    g34: LineSegment StartX=17.2232 StartY=-16.0875 StartZ=0 EndX=17.2232 EndY=-19.0875 EndZ=0
    g35: LineSegment StartX=28.8094 StartY=-19.0875 StartZ=0 EndX=17.2232 EndY=-19.0875 EndZ=0
    g36: LineSegment StartX=47.0443 StartY=-50.4712 StartZ=0 EndX=12.8789 EndY=-141.321 EndZ=0
    g37: LineSegment StartX=-195.441 StartY=-127.082 StartZ=0 EndX=-196.497 EndY=-129.89 EndZ=0
    g38: LineSegment StartX=85.2866 StartY=-36.8766 StartZ=0 EndX=78.9396 EndY=-53.7463 EndZ=0
    g39: LineSegment StartX=60.9579 StartY=-27.7053 StartZ=0 EndX=54.6191 EndY=-44.5532 EndZ=0
    g40: LineSegment StartX=68.0907 StartY=-82.7664 StartZ=0 EndX=61.7465 EndY=-99.6365 EndZ=0
    g41: LineSegment StartX=43.7619 StartY=-73.595 StartZ=0 EndX=37.426 EndY=-90.4435 EndZ=0
    g42: LineSegment StartX=50.885 StartY=-128.652 StartZ=0 EndX=44.5456 EndY=-145.522 EndZ=0
    g43: LineSegment StartX=26.5562 StartY=-119.481 StartZ=0 EndX=20.2251 EndY=-136.329 EndZ=0
    g44: LineSegment StartX=9.3071 StartY=-165.349 StartZ=0 EndX=2.97115 EndY=-182.197 EndZ=0
    g45: LineSegment StartX=33.6358 StartY=-174.52 StartZ=0 EndX=27.2917 EndY=-191.39 EndZ=0
  constraints (71):
    c: Block(g0)
    c: Block(g1)
    c: Block(g2)
    c: Block(g4)
    c: Block(g3)
    c: Block(g6)
    c: Block(g5)
    c: Block(g8)
    c: Block(g7)
    c: Weight(g9) = 1
    c: Equal(g9,g10)
    c: Equal(g9,g11)
    c: Equal(g9,g12)
    c: InternalAlignment(g9-g12 -> g13) x4
    c: InternalAlignment(g14,g13)
    c: InternalAlignment(g15,g13)
    c: Block(g16)
    c: Weight(g17) = 1
    c: Equal(g17,g18)
    c: Equal(g17,g19)
    c: InternalAlignment(g17,g20)
    c: InternalAlignment(g18,g20)
    c: InternalAlignment(g19,g20)
    c: InternalAlignment(g21,g20)
    c: InternalAlignment(g22,g20)
    c: Block(g20)
    c: Block(g23)
    c: Block(g24)
    c: Block(g25)
    c: Block(g26)
    c: Block(g27)
    c: Block(g28)
    c: Coincident(g29,g28)
    c: Coincident(g29,g0)
    c: Block(g13)
    c: Coincident(g31,g30)
    c: Coincident(g31,g28)
    c: Block(g31)
    c: Coincident(g32,g0)
    c: Vertical(g32)
    c: Coincident(g33,g32)
    c: Horizontal(g33)
    c: Coincident(g34,g33)
    c: Vertical(g34)
    c: Block(g33)
    c: Coincident(g35,g13)
    c: Coincident(g35,g34)
    c: Horizontal(g35)
    c: Coincident(g36,g13)
    c: Coincident(g36,g20)
    c: Coincident(g37,g20)
    c: Coincident(g37,g30)
    c: Block(g30)
    c: Coincident(g38,g1)
    c: Coincident(g38,g2)
    c: Coincident(g39,g1)
    c: Coincident(g39,g2)
    c: Coincident(g40,g3)
    c: Coincident(g40,g4)
    c: Coincident(g41,g3)
    c: Coincident(g41,g4)
    c: Coincident(g42,g5)
    c: Coincident(g42,g6)
    c: Coincident(g43,g5)
    c: Coincident(g43,g6)
    c: Coincident(g44,g7)
    c: Coincident(g44,g8)
    c: Coincident(g45,g7)
    c: Coincident(g45,g8)
    c: Distance(g30) = 256
    c: Distance(g33) = 100
FEATURE [Part::Extrusion] Extrude002
  Base = -> Sketch001
  Dir = (1,0,0)
  DirMode = 2
  FaceMakerClass = Part::FaceMakerBullseye
  LengthFwd = 8
  LengthRev = 0
  Solid = true
  Symmetric = false
FEATURE [Sketcher::SketchObject] Sketch002
  FullyConstrained = true
  sketch-geometry (20):
    g0: LineSegment StartX=-2.77179 StartY=-200.304 StartZ=0 EndX=5.22821 EndY=-200.304 EndZ=0
    g1: LineSegment StartX=5.22821 StartY=-200.304 StartZ=0 EndX=5.22821 EndY=-197.304 EndZ=0
    g2: LineSegment StartX=-2.77179 StartY=-200.304 StartZ=0 EndX=-2.77179 EndY=-197.304 EndZ=0
    g3: LineSegment StartX=5.22821 StartY=-197.304 StartZ=0 EndX=8.22821 EndY=-197.304 EndZ=0
    g4: LineSegment StartX=-2.77179 StartY=-197.304 StartZ=0 EndX=-5.77179 EndY=-197.304 EndZ=0
    g5: LineSegment StartX=19.2282 StartY=-203.304 StartZ=0 EndX=19.2282 EndY=-206.304 EndZ=0
    g6: LineSegment StartX=-16.7718 StartY=-203.304 StartZ=0 EndX=-16.7718 EndY=-206.304 EndZ=0
    g7: LineSegment StartX=-16.7718 StartY=-206.304 StartZ=0 EndX=19.2282 EndY=-206.304 EndZ=0
    g8: Circle CenterX=-16.7718 CenterY=-203.304 CenterZ=0 NormalX=0 NormalY=0 NormalZ=1 AngleXU=0 Radius=1
    g9: Circle CenterX=-5.77179 CenterY=-203.304 CenterZ=0 NormalX=0 NormalY=0 NormalZ=1 AngleXU=0 Radius=1
    g10: Circle CenterX=-5.77179 CenterY=-197.304 CenterZ=0 NormalX=0 NormalY=0 NormalZ=1 AngleXU=0 Radius=1
    g11: BSplineCurve PolesCount=3 KnotsCount=2 Degree=2 IsPeriodic=0
    g12: GeomPoint X=-16.7718 Y=-203.304 Z=0
    g13: GeomPoint X=-5.77179 Y=-197.304 Z=0
    g14: Circle CenterX=19.2282 CenterY=-203.304 CenterZ=0 NormalX=0 NormalY=0 NormalZ=1 AngleXU=0 Radius=1
    g15: Circle CenterX=8.22821 CenterY=-203.304 CenterZ=0 NormalX=0 NormalY=0 NormalZ=1 AngleXU=0 Radius=1
    g16: Circle CenterX=8.22821 CenterY=-197.304 CenterZ=0 NormalX=0 NormalY=0 NormalZ=1 AngleXU=0 Radius=1
    g17: BSplineCurve PolesCount=3 KnotsCount=2 Degree=2 IsPeriodic=0
    g18: GeomPoint X=19.2282 Y=-203.304 Z=0
    g19: GeomPoint X=8.22821 Y=-197.304 Z=0
  constraints (41):
    c: Horizontal(g0)
    c: Distance(g0) = 8
    c: Coincident(g1,g0)
    c: Vertical(g1)
    c: Distance(g1) = 3
    c: Coincident(g2,g0)
    c: Vertical(g2)
    c: Distance(g2) = 3
    c: Coincident(g3,g1)
    c: Horizontal(g3)
    c: Distance(g3) = 3
    c: Coincident(g4,g2)
    c: Horizontal(g4)
    c: Distance(g4) = 3
    c: Vertical(g5)
    c: Vertical(g6)
    c: Coincident(g7,g6)
    c: Coincident(g7,g5)
    c: Weight(g8) = 1
    c: Equal(g8,g9)
    c: Equal(g8,g10)
    c: Coincident(g11,g4)
    c: InternalAlignment(g8,g11)
    c: InternalAlignment(g9,g11)
    c: InternalAlignment(g10,g11)
    c: InternalAlignment(g12,g11)
    c: InternalAlignment(g13,g11)
    c: Coincident(g17,g5)
    c: Weight(g14) = 1
    c: Equal(g14,g15)
    c: Equal(g14,g16)
    c: Coincident(g17,g3)
    c: InternalAlignment(g14,g17)
    c: InternalAlignment(g15,g17)
    c: InternalAlignment(g16,g17)
    c: InternalAlignment(g18,g17)
    c: InternalAlignment(g19,g17)
    c: Block(g7)
    c: Block(g17)
    c: Block(g11)
    c: Block(g6)
FEATURE [Part::Extrusion] Extrude003
  Base = -> Sketch002
  Dir = (0,0,1)
  DirMode = 2
  FaceMakerClass = Part::FaceMakerBullseye
  LengthFwd = 260
  LengthRev = 0
  Solid = true
  Symmetric = false
FEATURE [Part::Extrusion] Extrude
  Base = -> Sketch
  Dir = (0,0,1)
  DirMode = 2
  FaceMakerClass = Part::FaceMakerBullseye
  LengthFwd = 14
  LengthRev = 0
  Solid = true
  Symmetric = false
